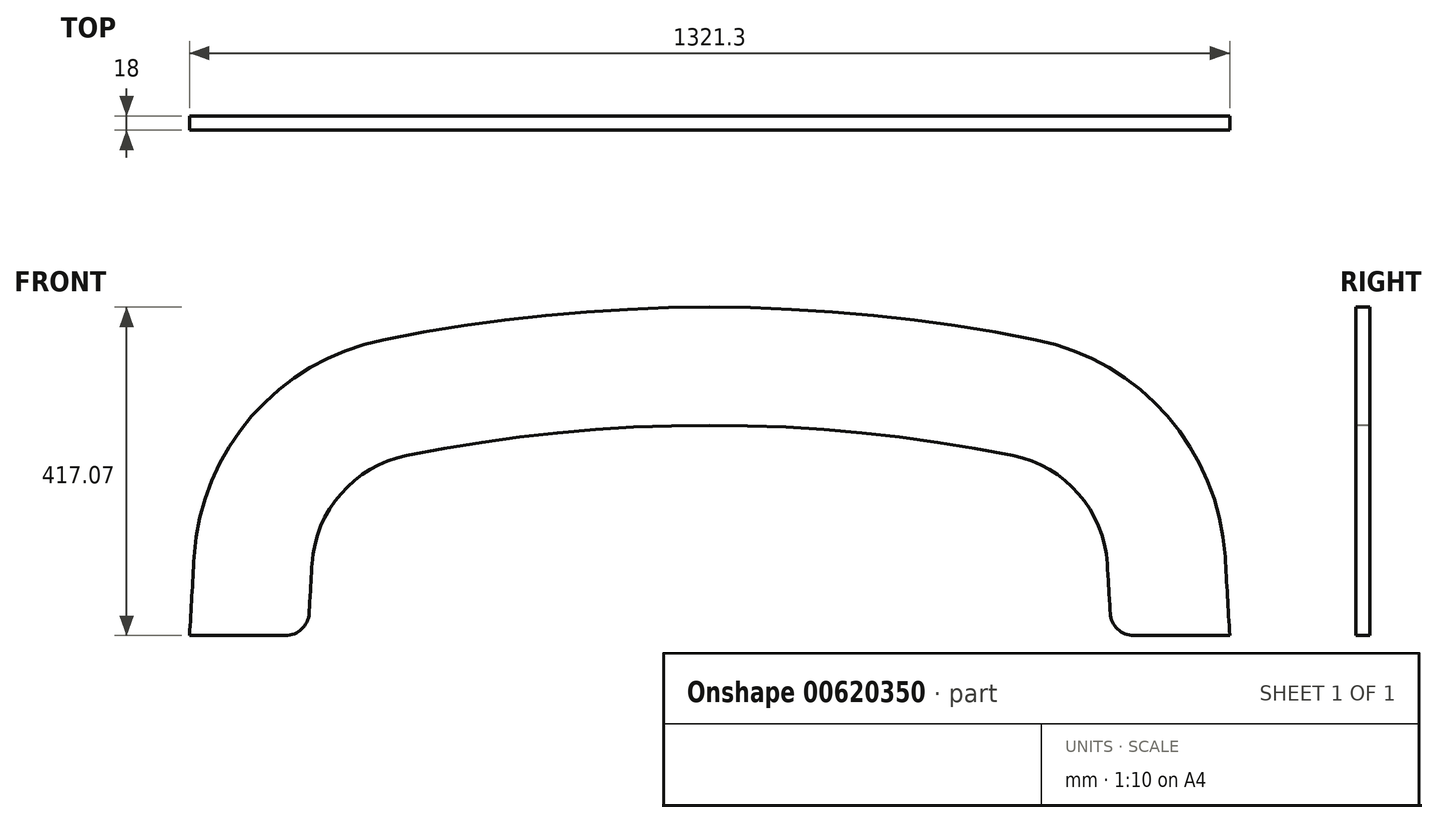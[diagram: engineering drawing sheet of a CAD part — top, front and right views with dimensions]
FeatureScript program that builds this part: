
annotation { "Feature Type Name" : "Feature", "Feature Type Description" : "" }
export const myFeature = defineFeature(function(context is Context, id is Id, definition is map)
    precondition{}
    {
        {
            var Q0;
            Q0=qCreatedBy(makeId("Front.planeOp"),FACE);
            var sketch = newSketch(context, id + "F0", { "sketchPlane" : qUnion([Q0])});
            skLineSegment(sketch, "E0", {"start": v(-685, 0) * mm, "end": v(685, 0) * mm});
            skLineSegment(sketch, "E1", {"start": v(-640, 1400) * mm, "end": v(640, 1400) * mm, "construction": true});
            skArc(sketch, "E2", {"start": v(640, 1400) * mm, "mid": v(0, 1500) * mm, "end": v(-640, 1400) * mm});
            skLineSegment(sketch, "E3", {"start": v(0, 1500) * mm, "end": v(0, 0) * mm, "construction": true});
            skPoint(sketch, "E3.endSnap0", {"position": v(0, 1500) * mm});
            skLineSegment(sketch, "E4", {"start": v(-685, 0) * mm, "end": v(-685, 200) * mm});
            skLineSegment(sketch, "E5", {"start": v(685, 0) * mm, "end": v(685, 200) * mm});
            skLineSegment(sketch, "E6", {"start": v(-685, 200) * mm, "end": v(685, 200) * mm, "construction": true});
            skArc(sketch, "E7", {"start": v(-640, 1400) * mm, "mid": v(-673.75, 800.42) * mm, "end": v(-685, 200) * mm});
            skArc(sketch, "E8", {"start": v(685, 200) * mm, "mid": v(673.75, 800.42) * mm, "end": v(640, 1400) * mm});
            skSolve(sketch);
        }
        {
            var Q0;
            Q0=makeQuery(id+"F0.imprint","IMPRINT",FACE,{"disambiguationData":[TD([[makeQuery(id+"F0.imprint","IMPRINT",EDGE,{"derivedFrom":sQuery(id+"F0.wireOp",EDGE,"E0")}),1.0]])]});
            extrude(context, id + "F1", {"entities" : qUnion([Q0]), "depth" : 18 * mm, "offsetDistance" : 25 * mm});
        }
        {
            var Q0;
            Q0=makeQuery(id+"F1.opExtrude","SWEPT_EDGE",EDGE,{"disambiguationData":[OSD([sQuery(id+"F0.wireOp",EDGE,"E2"),sQuery(id+"F0.wireOp",EDGE,"E7")])]});
            var Q1;
            Q1=makeQuery(id+"F1.opExtrude","SWEPT_EDGE",EDGE,{"disambiguationData":[OSD([sQuery(id+"F0.wireOp",EDGE,"E2"),sQuery(id+"F0.wireOp",EDGE,"E8")])]});
            fillet(context, id + "F2", {"entities" : qUnion([Q0, Q1]), "radius" : 300 * mm, "tangentPropagation" : true, "allowEdgeOverflow" : false});
        }
        {
            var Q0;
            Q0=makeQuery(id+"F1.opExtrude","CAP_FACE",FACE,{"disambiguationData":[OSD([sQuery(id+"F0.wireOp",EDGE,"E0"),sQuery(id+"F0.wireOp",EDGE,"E2"),sQuery(id+"F0.wireOp",EDGE,"E4"),sQuery(id+"F0.wireOp",EDGE,"E5"),sQuery(id+"F0.wireOp",EDGE,"E7"),sQuery(id+"F0.wireOp",EDGE,"E8")])],"isStart":false});
            var sketch = newSketch(context, id + "F3", { "sketchPlane" : qUnion([Q0])});
            skLineSegment(sketch, "E9", {"start": v(-660.65, 1082.93) * mm, "end": v(660.65, 1082.93) * mm, "construction": true});
            skArc(sketch, "E10.0", {"start": v(-505.1, 1173.73) * mm, "mid": v(-507.83, 1128.33) * mm, "end": v(-510.42, 1082.93) * mm});
            skArc(sketch, "E10.1", {"start": v(510.42, 1082.93) * mm, "mid": v(507.83, 1128.33) * mm, "end": v(505.1, 1173.73) * mm});
            skArc(sketch, "E10.2", {"start": v(505.1, 1173.73) * mm, "mid": v(468.5, 1263.05) * mm, "end": v(385.04, 1311.57) * mm});
            skArc(sketch, "E10.3", {"start": v(385.04, 1311.57) * mm, "mid": v(0, 1350) * mm, "end": v(-385.04, 1311.57) * mm});
            skArc(sketch, "E10.4", {"start": v(-385.04, 1311.57) * mm, "mid": v(-468.5, 1263.05) * mm, "end": v(-505.1, 1173.73) * mm});
            skLineSegment(sketch, "E11", {"start": v(-660.65, 1082.93) * mm, "end": v(-510.42, 1082.93) * mm});
            skLineSegment(sketch, "E12", {"start": v(510.42, 1082.93) * mm, "end": v(660.65, 1082.93) * mm});
            skSolve(sketch);
        }
        {
            var Q0;
            {var subQ2=sQuery(id+"F3.wireOp",EDGE,"RXioeDJg-sl7u-UEVi-XNgW-wfAgs17j1KTA");Q0=makeQuery(id+"F3.imprint","IMPRINT",FACE,{"disambiguationData":[TD([[makeQuery(id+"F3.imprint","IMPRINT",EDGE,{"derivedFrom":subQ2}),1.0]])]});}
            var Q1;
            Q1=makeQuery(id+"F3.imprint","IMPRINT",FACE,{"disambiguationData":[TD([[makeQuery(id+"F3.imprint","IMPRINT",EDGE,{"derivedFrom":sQuery(id+"F3.wireOp",EDGE,"E10.0")}),1.0]])]});
            extrude(context, id + "F4", {"entities" : qUnion([Q0, Q1]), "operationType" : NewBodyOperationType.REMOVE, "endBound" : BoundingType.THROUGH_ALL, "oppositeDirection" : true, "depth" : 25 * mm, "offsetDistance" : 25 * mm});
        }
        {
            var Q0;
            Q0=makeQuery(id+"F4.boolean.opBoolean","COPY",EDGE,{"derivedFrom":makeQuery(id+"F4.opExtrude","SWEPT_EDGE",EDGE,{"disambiguationData":[OSD([sQuery(id+"F0.wireOp",EDGE,"E7"),sQuery(id+"F3.wireOp",EDGE,"RXioeDJg-sl7u-UEVi-XNgW-wfAgs17j1KTA")])]})});
            var Q1;
            Q1=makeQuery(id+"F4.boolean.opBoolean","COPY",EDGE,{"derivedFrom":makeQuery(id+"F4.opExtrude","SWEPT_EDGE",EDGE,{"disambiguationData":[OSD([sQuery(id+"F0.wireOp",EDGE,"E8"),sQuery(id+"F3.wireOp",EDGE,"RXioeDJg-sl7u-UEVi-XNgW-wfAgs17j1KTA")])]})});
            var Q2;
            Q2=makeQuery(id+"F4.boolean.opBoolean","COPY",EDGE,{"derivedFrom":makeQuery(id+"F4.opExtrude","SWEPT_EDGE",EDGE,{"disambiguationData":[OSD([sQuery(id+"F3.wireOp",EDGE,"E10.0"),sQuery(id+"F3.wireOp",EDGE,"E11")])]})});
            var Q3;
            Q3=makeQuery(id+"F4.boolean.opBoolean","COPY",EDGE,{"derivedFrom":makeQuery(id+"F4.opExtrude","SWEPT_EDGE",EDGE,{"disambiguationData":[OSD([sQuery(id+"F3.wireOp",EDGE,"E10.1"),sQuery(id+"F3.wireOp",EDGE,"E12")])]})});
            fillet(context, id + "F5", {"entities" : qUnion([Q0, Q1, Q2, Q3]), "radius" : 30 * mm, "tangentPropagation" : true, "allowEdgeOverflow" : false});
        }
    });
